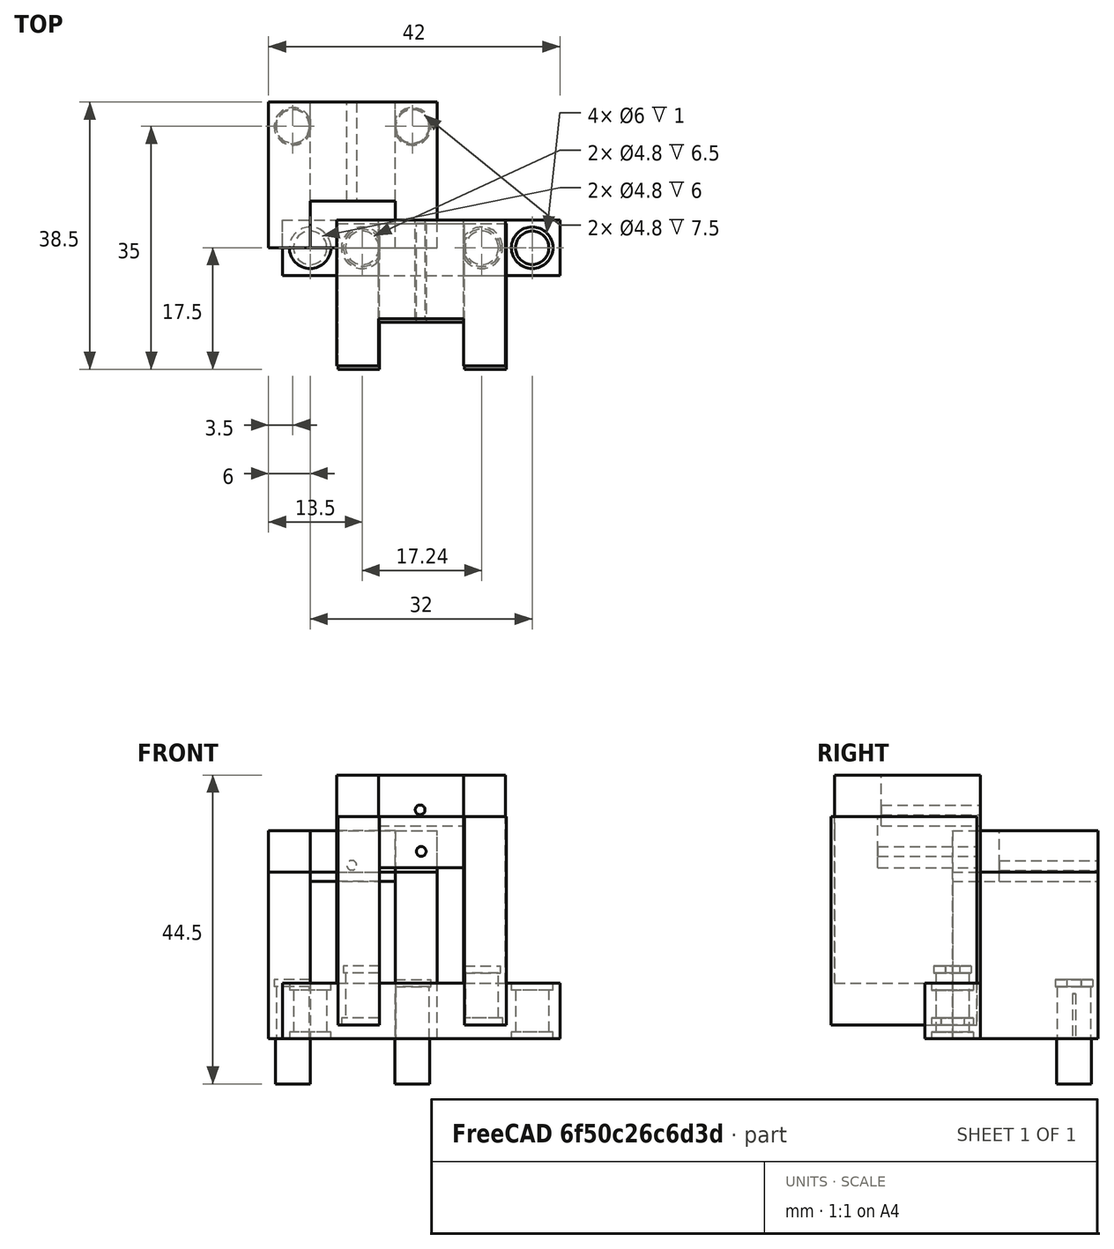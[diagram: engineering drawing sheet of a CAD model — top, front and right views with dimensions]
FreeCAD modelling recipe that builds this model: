
FCSTD DOCUMENT  (FreeCAD 0.20R29177 +426 (Git))
Label: servoBox
License: All rights reserved
LicenseURL: http://en.wikipedia.org/wiki/All_rights_reserved
objects: Part::Cylinder×13, Part::Box×12, Part::MultiFuse×11, Part::Cut×9, Part::Feature×2, Part::MultiCommon×2, Part::FeaturePython×1, Mesh::Feature×1
note: 49 computed .brp shape members not serialized (recipe doc carries the construction recipe); baked Part::Feature solids carry a one-line shape summary decoded from their .brp

FEATURE [Part::Box] Box  label="servo"
  AttacherType = Attacher::AttachEngine3D
  Height = 22.68
  Length = 12.25
  Placement = pos=(0,-1,0) rot=(0,0,1;0rad)
  Width = 23.78
FEATURE [Part::Box] Box002  label="Cube"
  AttacherType = Attacher::AttachEngine3D
  Height = 24
  Length = 24.3
  Placement = pos=(-6,0,0) rot=(0,0,1;0rad)
  Width = 21
FEATURE [Part::Cylinder] Cylinder
  Angle = 360
  AttacherType = Attacher::AttachEngine3D
  FirstAngle = 0
  Height = 13
  Placement = pos=(-2.5,17.5,-6.5) rot=(0,0,1;0rad)
  Radius = 2.5
  SecondAngle = 0
FEATURE [Part::Cylinder] Cylinder001
  Angle = 360
  AttacherType = Attacher::AttachEngine3D
  FirstAngle = 0
  Height = 13
  Placement = pos=(14.74,17.5,-6.5) rot=(0,0,1;0rad)
  Radius = 2.5
  SecondAngle = 0
FEATURE [Part::Cut] Cut
  Base = -> Box002
  Tool = -> Box
FEATURE [Part::MultiFuse] Fusion
  Shapes = -> [Cylinder,Cylinder001,Cut]
FEATURE [Part::Box] Box003  label="servo001"
  AttacherType = Attacher::AttachEngine3D
  Height = 22.68
  Length = 12.25
  Placement = pos=(0,-1,0) rot=(0,0,1;0rad)
  Width = 23.78
FEATURE [Part::Box] Box004  label="Cube001"
  AttacherType = Attacher::AttachEngine3D
  Height = 24
  Length = 24.3
  Placement = pos=(-6,0,0) rot=(0,0,1;0rad)
  Width = 21
FEATURE [Part::Cut] Cut001
  Base = -> Box004
  Tool = -> Box003
FEATURE [Part::Feature] _459001  label="pin"
  Placement = pos=(-2.8,0,0) rot=(0,1,0;1.5708rad)
  shape: bbox 6.401 x 6.401 x 16 mm, 1216 faces, 0 solids (baked)
FEATURE [Part::Box] Box005  label="Cube002"
  AttacherType = Attacher::AttachEngine3D
  Height = 10
  Length = 10
  Placement = pos=(-8,-6,-10.9) rot=(0,1,0;0rad)
  Width = 10
FEATURE [Part::MultiCommon] Common
  Placement = pos=(0.3,17.5,1) rot=(0,0,1;0rad)
  Shapes = -> [_459001,Box005]
FEATURE [Part::Box] Box006  label="Cube003"
  AttacherType = Attacher::AttachEngine3D
  Height = 10
  Length = 10
  Placement = pos=(-8,-6,-10.9) rot=(0,1,0;0rad)
  Width = 10
FEATURE [Part::Feature] _459002  label="pin001"
  Placement = pos=(-2.8,0,0) rot=(0,1,0;1.5708rad)
  shape: bbox 6.401 x 6.401 x 16 mm, 1216 faces, 0 solids (baked)
FEATURE [Part::MultiCommon] Common001
  Placement = pos=(17.55,17.5,1) rot=(0,0,1;0rad)
  Shapes = -> [_459002,Box006]
FEATURE [Part::MultiFuse] Fusion001
  Shapes = -> [Common,Common001]
FEATURE [Part::Box] Box007  label="Cube004"
  AttacherType = Attacher::AttachEngine3D
  Height = 10
  Length = 12.25
  Placement = pos=(0,-3.25,22) rot=(0,0,1;0rad)
  Width = 10
FEATURE [Part::MultiFuse] Fusion002  label="servo002"
  Shapes = -> [Box003,Box007]
FEATURE [Part::Box] Box008  label="Cube005"
  AttacherType = Attacher::AttachEngine3D
  Height = 30
  Length = 24.3
  Placement = pos=(-6,0,0) rot=(0,0,1;0rad)
  Width = 21
FEATURE [Part::MultiFuse] Fusion003
  Shapes = -> [Box007,Fusion002]
FEATURE [Part::Cut] Cut002
  Base = -> Box008
  Tool = -> Fusion003
FEATURE [Part::Cylinder] Cylinder002
  Angle = 360
  AttacherType = Attacher::AttachEngine3D
  FirstAngle = 0
  Height = 16
  Placement = pos=(6,22,25) rot=(1,0,0;1.5708rad)
  Radius = 0.7
  SecondAngle = 0
FEATURE [Part::Cut] Cut003
  Base = -> Cut002
  Tool = -> Cylinder002
FEATURE [Part::Cylinder] Cylinder003
  Angle = 360
  AttacherType = Attacher::AttachEngine3D
  FirstAngle = 0
  Height = 13
  Placement = pos=(-2.5,17.5,-6.5) rot=(0,0,1;0rad)
  Radius = 2.4
  SecondAngle = 0
FEATURE [Part::Cylinder] Cylinder004
  Angle = 360
  AttacherType = Attacher::AttachEngine3D
  FirstAngle = 0
  Height = 13
  Placement = pos=(14.74,17.5,-6.5) rot=(0,0,1;0rad)
  Radius = 2.4
  SecondAngle = 0
FEATURE [Part::Cylinder] Cylinder005
  Angle = 360
  AttacherType = Attacher::AttachEngine3D
  FirstAngle = 0
  Height = 1
  Placement = pos=(-2.5,17.5,6.5) rot=(0,0,1;0rad)
  Radius = 2.7
  SecondAngle = 0
FEATURE [Part::Cylinder] Cylinder006
  Angle = 360
  AttacherType = Attacher::AttachEngine3D
  FirstAngle = 0
  Height = 1
  Placement = pos=(14.74,17.5,6.5) rot=(0,0,1;0rad)
  Radius = 2.7
  SecondAngle = 0
FEATURE [Part::MultiFuse] Fusion004
  Placement = pos=(0,0,1) rot=(0,0,1;0rad)
  Shapes = -> [Cylinder003,Cylinder004,Cylinder005,Cylinder006]
FEATURE [Part::Cut] Cut004
  Base = -> Cut003
  Tool = -> Fusion004
FEATURE [Part::Cylinder] Cylinder007
  Angle = 360
  AttacherType = Attacher::AttachEngine3D
  FirstAngle = 0
  Height = 1.1
  Placement = pos=(14.74,17.5,-0.1) rot=(0,0,1;0rad)
  Radius = 3
  SecondAngle = 0
FEATURE [Part::Cylinder] Cylinder008
  Angle = 360
  AttacherType = Attacher::AttachEngine3D
  FirstAngle = 0
  Height = 1.1
  Placement = pos=(-2.5,17.5,-0.1) rot=(0,0,1;0rad)
  Radius = 3
  SecondAngle = 0
FEATURE [Part::MultiFuse] Fusion005
  Shapes = -> [Cylinder007,Cylinder008]
FEATURE [Part::MultiFuse] Fusion006
  Shapes = -> [Fusion004,Fusion005]
FEATURE [Part::Cut] Cut005
  Base = -> Cut003
  Placement = pos=(10,-17.5,2) rot=(0,0,1;0rad)
  Tool = -> Fusion006
FEATURE [Part::Box] Box009  label="servo003"
  AttacherType = Attacher::AttachEngine3D
  Height = 22.68
  Length = 12.25
  Placement = pos=(0,-1,0) rot=(0,0,1;0rad)
  Width = 23.78
FEATURE [Part::Box] Box010  label="Cube006"
  AttacherType = Attacher::AttachEngine3D
  Height = 10
  Length = 12.25
  Placement = pos=(0,-3.25,22) rot=(0,0,1;0rad)
  Width = 10
FEATURE [Part::Box] Box011  label="Cube007"
  AttacherType = Attacher::AttachEngine3D
  Height = 30
  Length = 24.3
  Placement = pos=(-6,0,0) rot=(0,0,1;0rad)
  Width = 21
FEATURE [Part::Cylinder] Cylinder009
  Angle = 360
  AttacherType = Attacher::AttachEngine3D
  FirstAngle = 0
  Height = 16
  Placement = pos=(6,22,25) rot=(1,0,0;1.5708rad)
  Radius = 0.7
  SecondAngle = 0
FEATURE [Part::MultiFuse] Fusion007  label="servo004"
  Shapes = -> [Box009,Box010]
FEATURE [Part::MultiFuse] Fusion008
  Shapes = -> [Box010,Fusion007]
FEATURE [Part::Cut] Cut006
  Base = -> Box011
  Tool = -> Fusion008
FEATURE [Part::Cut] Cut007  label="box"
  Base = -> Cut006
  Placement = pos=(9.85,-17,8) rot=(0,0,1;0rad)
  Tool = -> Cylinder009
FEATURE [Part::Box] Box012  label="Cube008"
  AttacherType = Attacher::AttachEngine3D
  Height = 8
  Length = 40
  Placement = pos=(-4,-4,0) rot=(0,0,1;0rad)
  Width = 8
FEATURE [Part::Cylinder] Cylinder011
  Angle = 360
  AttacherType = Attacher::AttachEngine3D
  FirstAngle = 0
  Height = 1
  Radius = 3
  SecondAngle = 0
FEATURE [Part::Cylinder] Cylinder012
  Angle = 360
  AttacherType = Attacher::AttachEngine3D
  FirstAngle = 0
  Height = 1
  Placement = pos=(0,0,7) rot=(0,0,1;0rad)
  Radius = 3
  SecondAngle = 0
FEATURE [Part::Cylinder] Cylinder013
  Angle = 360
  AttacherType = Attacher::AttachEngine3D
  FirstAngle = 0
  Height = 8
  Radius = 2.4
  SecondAngle = 0
FEATURE [Part::MultiFuse] Fusion009
  Shapes = -> [Cylinder011,Cylinder012,Cylinder013]
FEATURE [Part::FeaturePython] Array  # Draft array (typed FeaturePython)
  AlwaysSyncPlacement = false
  Angle = 360
  ArrayType = 0
  Axis = (0,0,1)
  Base = -> Fusion009
  Center = (0,0,0)
  Count = 2
  ExpandArray = false
  Fuse = false
  IntervalAxis = (0,0,0)
  IntervalX = (32,0,0)
  IntervalY = (0,100,0)
  IntervalZ = (0,0,100)
  NumberCircles = 3
  NumberPolar = 5
  NumberX = 2
  NumberY = 1
  NumberZ = 1
  PlacementList = 2 placements: [(0,0,0),(32,0,0)]
  RadialDistance = 50
  ScaleList = (2) [(1,1,1),(1,1,1)]
  Symmetry = 1
  TangentialDistance = 25
FEATURE [Part::Cut] Cut008
  Base = -> Box012
  Tool = -> Array
FEATURE [Part::MultiFuse] Fusion010
  Shapes = -> [Cut008,Cut007]
FEATURE [Mesh::Feature] Mesh  label="Fusion010 (Meshed)"
